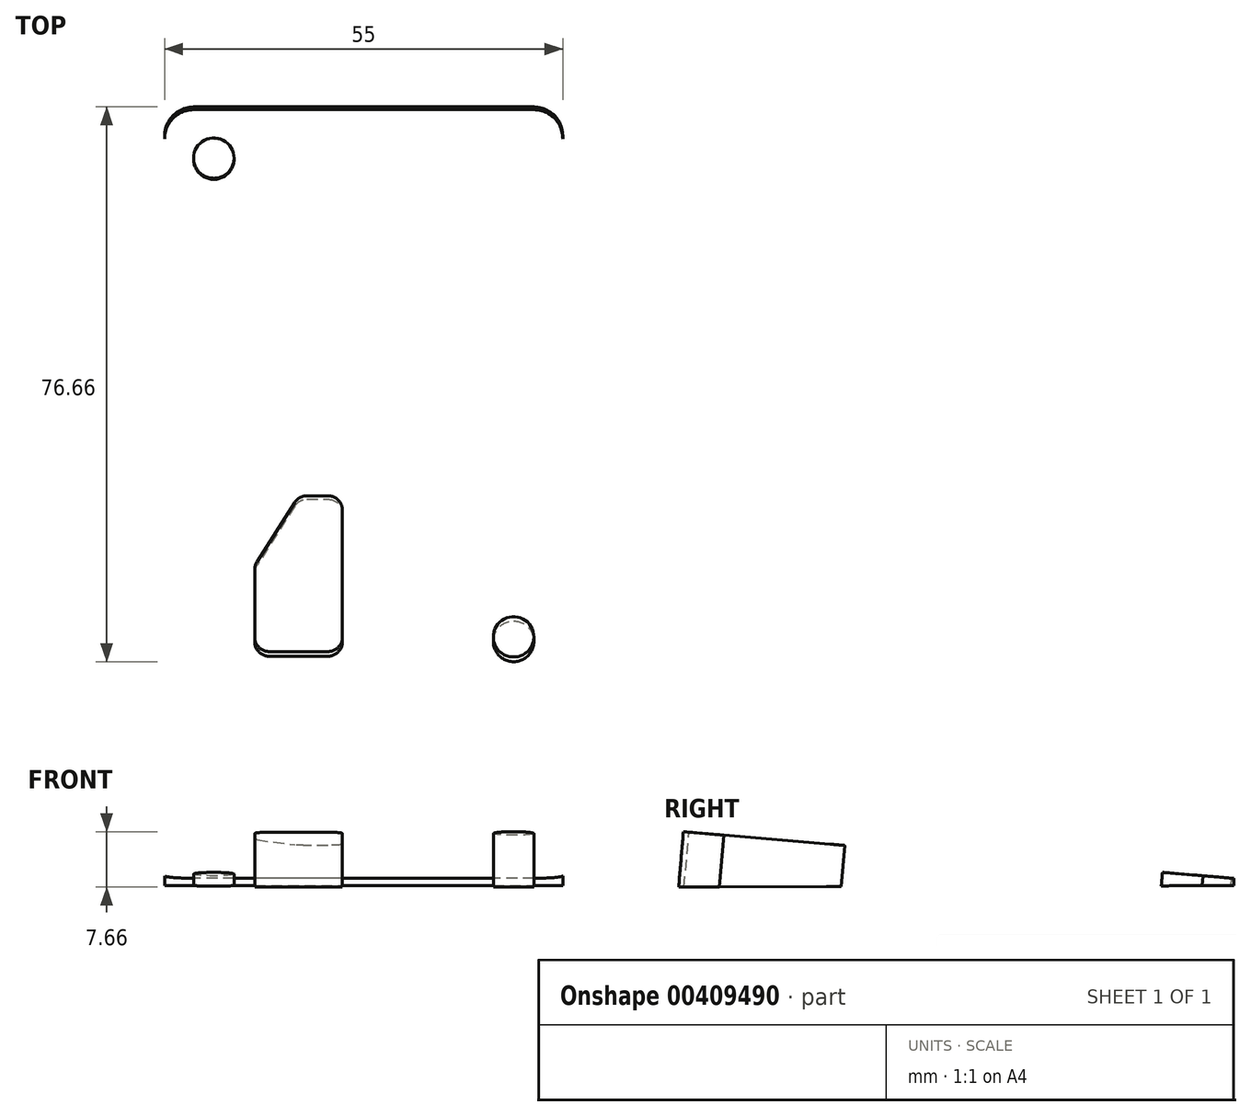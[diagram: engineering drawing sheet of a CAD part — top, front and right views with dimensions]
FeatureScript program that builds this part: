
annotation { "Feature Type Name" : "Feature", "Feature Type Description" : "" }
export const myFeature = defineFeature(function(context is Context, id is Id, definition is map)
    precondition{}
    {
        {
            var Q0;
            Q0=qCreatedBy(makeId("Right.planeOp"),FACE);
            var sketch = newSketch(context, id + "F0", { "sketchPlane" : qUnion([Q0])});
            skLineSegment(sketch, "E0", {"start": v(-0.45, -1.5) * mm, "end": v(-0.45, 6.5) * mm});
            skLineSegment(sketch, "E1", {"start": v(-0.45, 6.5) * mm, "end": v(79.55, -0.3) * mm});
            skLineSegment(sketch, "E2", {"start": v(79.55, -0.3) * mm, "end": v(79.55, -1.3) * mm});
            skLineSegment(sketch, "E3", {"start": v(79.55, -1.3) * mm, "end": v(-0.45, -1.5) * mm});
            skSolve(sketch);
        }
        {
            var Q0;
            Q0=makeQuery(id+"F0.imprint","IMPRINT",FACE,{"disambiguationData":[TD([[makeQuery(id+"F0.imprint","IMPRINT",EDGE,{"derivedFrom":sQuery(id+"F0.wireOp",EDGE,"E0")}),-1.0]])]});
            extrude(context, id + "F1", {"entities" : qUnion([Q0]), "depth" : 55 * mm});
        }
        {
            var Q0;
            Q0=makeQuery(id+"F1.opExtrude","CAP_EDGE",EDGE,{"disambiguationData":[OSD([sQuery(id+"F0.wireOp",EDGE,"E0")])],"isStart":true});
            var Q1;
            Q1=makeQuery(id+"F1.opExtrude","CAP_EDGE",EDGE,{"disambiguationData":[OSD([sQuery(id+"F0.wireOp",EDGE,"E0")])],"isStart":false});
            var Q2;
            Q2=makeQuery(id+"F1.opExtrude","CAP_EDGE",EDGE,{"disambiguationData":[OSD([sQuery(id+"F0.wireOp",EDGE,"E2")])],"isStart":true});
            var Q3;
            Q3=makeQuery(id+"F1.opExtrude","CAP_EDGE",EDGE,{"disambiguationData":[OSD([sQuery(id+"F0.wireOp",EDGE,"E2")])],"isStart":false});
            fillet(context, id + "F2", {"entities" : qUnion([Q0, Q1, Q2, Q3]), "radius" : 4 * mm, "tangentPropagation" : true, "allowEdgeOverflow" : false});
        }
        {
            var Q0;
            Q0=makeQuery(id+"F1.opExtrude","SWEPT_FACE",FACE,{"disambiguationData":[OSD([sQuery(id+"F0.wireOp",EDGE,"E1")])]});
            var sketch = newSketch(context, id + "F3", { "sketchPlane" : qUnion([Q0])});
            skLineSegment(sketch, "E4.bottom", {"start": v(51, -1) * mm, "end": v(4, -1) * mm});
            skLineSegment(sketch, "E4.top", {"start": v(51, 79) * mm, "end": v(4, 79) * mm});
            skLineSegment(sketch, "E4.left", {"start": v(55, 3) * mm, "end": v(55, 75) * mm});
            skLineSegment(sketch, "E4.right", {"start": v(0, 3) * mm, "end": v(0, 75) * mm});
            skCircle(sketch, "E5", {"center": v(6.8, 5.8) * mm, "radius": 2.8 * mm});
            skCircle(sketch, "E6.MirrorC", {"center": v(48.2, 5.8) * mm, "radius": 2.8 * mm});
            skCircle(sketch, "E7.MirrorC", {"center": v(48.2, 72.2) * mm, "radius": 2.8 * mm});
            skCircle(sketch, "E8.MirrorC", {"center": v(6.8, 72.2) * mm, "radius": 2.8 * mm});
            skLineSegment(sketch, "E9.bottom", {"start": v(35.5, 29) * mm, "end": v(19.5, 29) * mm});
            skLineSegment(sketch, "E9.top", {"start": v(35.5, 49) * mm, "end": v(19.5, 49) * mm});
            skLineSegment(sketch, "E9.left", {"start": v(37.5, 31) * mm, "end": v(37.5, 47) * mm});
            skLineSegment(sketch, "E9.right", {"start": v(17.5, 31) * mm, "end": v(17.5, 47) * mm});
            skArc(sketch, "E10.filletArc", {"start": v(19.5, 49) * mm, "mid": v(18.09, 48.42) * mm, "end": v(17.5, 47) * mm});
            skArc(sketch, "E11.filletArc", {"start": v(37.5, 47) * mm, "mid": v(36.91, 48.42) * mm, "end": v(35.5, 49) * mm});
            skArc(sketch, "E12.filletArc", {"start": v(17.5, 31) * mm, "mid": v(18.09, 29.59) * mm, "end": v(19.5, 29) * mm});
            skArc(sketch, "E13.filletArc", {"start": v(35.5, 29) * mm, "mid": v(36.91, 29.59) * mm, "end": v(37.5, 31) * mm});
            skArc(sketch, "E14.filletArc", {"start": v(0, 3) * mm, "mid": v(1.17, 0.17) * mm, "end": v(4, -1) * mm});
            skArc(sketch, "E15.filletArc", {"start": v(51, -1) * mm, "mid": v(53.83, 0.17) * mm, "end": v(55, 3) * mm});
            skArc(sketch, "E16.filletArc", {"start": v(4, 79) * mm, "mid": v(1.17, 77.83) * mm, "end": v(0, 75) * mm});
            skArc(sketch, "E17.filletArc", {"start": v(55, 75) * mm, "mid": v(53.83, 77.83) * mm, "end": v(51, 79) * mm});
            skLineSegment(sketch, "E18.bottom", {"start": v(14.45, 74.25) * mm, "end": v(22.57, 74.25) * mm});
            skLineSegment(sketch, "E18.right", {"start": v(24.57, 72.25) * mm, "end": v(24.57, 54.64) * mm});
            skArc(sketch, "E19.filletArc", {"start": v(14.45, 74.25) * mm, "mid": v(13.04, 73.67) * mm, "end": v(12.45, 72.25) * mm});
            skArc(sketch, "E20.filletArc", {"start": v(22.57, 52.64) * mm, "mid": v(23.98, 53.23) * mm, "end": v(24.57, 54.64) * mm});
            skArc(sketch, "E21.filletArc", {"start": v(24.57, 72.25) * mm, "mid": v(23.98, 73.67) * mm, "end": v(22.57, 74.25) * mm});
            skLineSegment(sketch, "E22", {"start": v(12.45, 72.25) * mm, "end": v(12.45, 62.83) * mm});
            skLineSegment(sketch, "E23", {"start": v(12.76, 61.76) * mm, "end": v(17.98, 53.57) * mm});
            skLineSegment(sketch, "E24", {"start": v(22.57, 52.64) * mm, "end": v(19.66, 52.64) * mm});
            skArc(sketch, "E25.filletArc", {"start": v(12.45, 62.83) * mm, "mid": v(12.53, 62.28) * mm, "end": v(12.76, 61.76) * mm});
            skArc(sketch, "E26.filletArc", {"start": v(17.98, 53.57) * mm, "mid": v(18.7, 52.89) * mm, "end": v(19.66, 52.64) * mm});
            skLineSegment(sketch, "E27.MirrorCS", {"start": v(30.43, 72.25) * mm, "end": v(30.43, 54.64) * mm});
            skLineSegment(sketch, "E28.MirrorCS", {"start": v(42.55, 72.25) * mm, "end": v(42.55, 62.83) * mm});
            skArc(sketch, "E29.MirrorCS", {"start": v(40.55, 74.25) * mm, "mid": v(41.96, 73.67) * mm, "end": v(42.55, 72.25) * mm});
            skLineSegment(sketch, "E30.MirrorCS", {"start": v(40.55, 74.25) * mm, "end": v(32.43, 74.25) * mm});
            skArc(sketch, "E31.MirrorCS", {"start": v(30.43, 72.25) * mm, "mid": v(31.02, 73.67) * mm, "end": v(32.43, 74.25) * mm});
            skArc(sketch, "E32.MirrorCS", {"start": v(32.43, 52.64) * mm, "mid": v(31.02, 53.23) * mm, "end": v(30.43, 54.64) * mm});
            skLineSegment(sketch, "E33.MirrorCS", {"start": v(32.43, 52.64) * mm, "end": v(35.34, 52.64) * mm});
            skLineSegment(sketch, "E34.MirrorCS", {"start": v(42.24, 61.76) * mm, "end": v(37.02, 53.57) * mm});
            skArc(sketch, "E35.MirrorCS", {"start": v(42.55, 62.83) * mm, "mid": v(42.47, 62.28) * mm, "end": v(42.24, 61.76) * mm});
            skArc(sketch, "E36.MirrorCS", {"start": v(37.02, 53.57) * mm, "mid": v(36.3, 52.89) * mm, "end": v(35.34, 52.64) * mm});
            skLineSegment(sketch, "E37.MirrorCS", {"start": v(30.43, 5.75) * mm, "end": v(30.43, 23.36) * mm});
            skArc(sketch, "E38.MirrorCS", {"start": v(32.43, 25.36) * mm, "mid": v(31.02, 24.78) * mm, "end": v(30.43, 23.36) * mm});
            skLineSegment(sketch, "E39.MirrorCS", {"start": v(32.43, 25.36) * mm, "end": v(35.34, 25.36) * mm});
            skArc(sketch, "E40.MirrorCS", {"start": v(37.02, 24.44) * mm, "mid": v(36.3, 25.12) * mm, "end": v(35.34, 25.36) * mm});
            skLineSegment(sketch, "E41.MirrorCS", {"start": v(42.24, 16.24) * mm, "end": v(37.02, 24.44) * mm});
            skArc(sketch, "E42.MirrorCS", {"start": v(42.55, 15.17) * mm, "mid": v(42.47, 15.73) * mm, "end": v(42.24, 16.24) * mm});
            skLineSegment(sketch, "E43.MirrorCS", {"start": v(42.55, 5.75) * mm, "end": v(42.55, 15.17) * mm});
            skArc(sketch, "E44.MirrorCS", {"start": v(30.43, 5.75) * mm, "mid": v(31.02, 4.34) * mm, "end": v(32.43, 3.75) * mm});
            skLineSegment(sketch, "E45.MirrorCS", {"start": v(40.55, 3.75) * mm, "end": v(32.43, 3.75) * mm});
            skArc(sketch, "E46.MirrorCS", {"start": v(40.55, 3.75) * mm, "mid": v(41.96, 4.34) * mm, "end": v(42.55, 5.75) * mm});
            skArc(sketch, "E47.MirrorCS", {"start": v(24.57, 5.75) * mm, "mid": v(23.98, 4.34) * mm, "end": v(22.57, 3.75) * mm});
            skLineSegment(sketch, "E48.MirrorCS", {"start": v(24.57, 5.75) * mm, "end": v(24.57, 23.36) * mm});
            skLineSegment(sketch, "E49.MirrorCS", {"start": v(14.45, 3.75) * mm, "end": v(22.57, 3.75) * mm});
            skArc(sketch, "E50.MirrorCS", {"start": v(14.45, 3.75) * mm, "mid": v(13.04, 4.34) * mm, "end": v(12.45, 5.75) * mm});
            skLineSegment(sketch, "E51.MirrorCS", {"start": v(12.45, 5.75) * mm, "end": v(12.45, 15.17) * mm});
            skArc(sketch, "E52.MirrorCS", {"start": v(12.45, 15.17) * mm, "mid": v(12.53, 15.73) * mm, "end": v(12.76, 16.24) * mm});
            skLineSegment(sketch, "E53.MirrorCS", {"start": v(12.76, 16.24) * mm, "end": v(17.98, 24.44) * mm});
            skArc(sketch, "E54.MirrorCS", {"start": v(22.57, 25.36) * mm, "mid": v(23.98, 24.78) * mm, "end": v(24.57, 23.36) * mm});
            skLineSegment(sketch, "E55.MirrorCS", {"start": v(22.57, 25.36) * mm, "end": v(19.66, 25.36) * mm});
            skArc(sketch, "E56.MirrorCS", {"start": v(17.98, 24.44) * mm, "mid": v(18.7, 25.12) * mm, "end": v(19.66, 25.36) * mm});
            skLineSegment(sketch, "E57.bottom", {"start": v(9.25, 52.5) * mm, "end": v(10.5, 52.5) * mm});
            skLineSegment(sketch, "E57.top", {"start": v(9.25, 23.36) * mm, "end": v(10.5, 23.36) * mm});
            skLineSegment(sketch, "E57.left", {"start": v(4.25, 47.5) * mm, "end": v(4.25, 28.36) * mm});
            skLineSegment(sketch, "E57.right", {"start": v(15.5, 47.5) * mm, "end": v(15.5, 28.36) * mm});
            skArc(sketch, "E58.filletArc", {"start": v(4.25, 28.36) * mm, "mid": v(5.71, 24.83) * mm, "end": v(9.25, 23.36) * mm});
            skArc(sketch, "E59.filletArc", {"start": v(10.5, 23.36) * mm, "mid": v(14.04, 24.83) * mm, "end": v(15.5, 28.36) * mm});
            skArc(sketch, "E60.filletArc", {"start": v(9.25, 52.5) * mm, "mid": v(5.71, 51.04) * mm, "end": v(4.25, 47.5) * mm});
            skArc(sketch, "E61.filletArc", {"start": v(15.5, 47.5) * mm, "mid": v(14.04, 51.04) * mm, "end": v(10.5, 52.5) * mm});
            skLineSegment(sketch, "E62.MirrorCS", {"start": v(50.75, 47.5) * mm, "end": v(50.75, 28.36) * mm});
            skLineSegment(sketch, "E63.MirrorCS", {"start": v(39.5, 47.5) * mm, "end": v(39.5, 28.36) * mm});
            skArc(sketch, "E64.MirrorCS", {"start": v(39.5, 47.5) * mm, "mid": v(40.96, 51.04) * mm, "end": v(44.5, 52.5) * mm});
            skLineSegment(sketch, "E65.MirrorCS", {"start": v(45.75, 52.5) * mm, "end": v(44.5, 52.5) * mm});
            skArc(sketch, "E66.MirrorCS", {"start": v(45.75, 52.5) * mm, "mid": v(49.29, 51.04) * mm, "end": v(50.75, 47.5) * mm});
            skArc(sketch, "E67.MirrorCS", {"start": v(50.75, 28.36) * mm, "mid": v(49.29, 24.83) * mm, "end": v(45.75, 23.36) * mm});
            skArc(sketch, "E68.MirrorCS", {"start": v(44.5, 23.36) * mm, "mid": v(40.96, 24.83) * mm, "end": v(39.5, 28.36) * mm});
            skLineSegment(sketch, "E69.MirrorCS", {"start": v(45.75, 23.36) * mm, "end": v(44.5, 23.36) * mm});
            skSolve(sketch);
        }
        {
            var Q0;
            Q0=makeQuery(id+"F3.imprint","IMPRINT",FACE,{"disambiguationData":[TD([[makeQuery(id+"F3.imprint","IMPRINT",EDGE,{"derivedFrom":sQuery(id+"F3.wireOp",EDGE,"E57.bottom")}),-1.0]])]});
            var Q1;
            Q1=makeQuery(id+"F3.imprint","IMPRINT",FACE,{"disambiguationData":[TD([[makeQuery(id+"F3.imprint","IMPRINT",EDGE,{"derivedFrom":sQuery(id+"F3.wireOp",EDGE,"E9.bottom")}),-1.0]])]});
            var Q2;
            Q2=makeQuery(id+"F3.imprint","IMPRINT",FACE,{"disambiguationData":[TD([[makeQuery(id+"F3.imprint","IMPRINT",EDGE,{"derivedFrom":sQuery(id+"F3.wireOp",EDGE,"E62.MirrorCS")}),-1.0]])]});
            var Q3;
            Q3=makeQuery(id+"F3.imprint","IMPRINT",FACE,{"disambiguationData":[TD([[makeQuery(id+"F3.imprint","IMPRINT",EDGE,{"derivedFrom":sQuery(id+"F3.wireOp",EDGE,"E47.MirrorCS")}),-1.0]])]});
            var Q4;
            Q4=makeQuery(id+"F3.imprint","IMPRINT",FACE,{"disambiguationData":[TD([[makeQuery(id+"F3.imprint","IMPRINT",EDGE,{"derivedFrom":sQuery(id+"F3.wireOp",EDGE,"E37.MirrorCS")}),-1.0]])]});
            var Q5;
            Q5=makeQuery(id+"F3.imprint","IMPRINT",FACE,{"disambiguationData":[TD([[makeQuery(id+"F3.imprint","IMPRINT",EDGE,{"derivedFrom":sQuery(id+"F3.wireOp",EDGE,"E27.MirrorCS")}),1.0]])]});
            var Q6;
            Q6=makeQuery(id+"F3.imprint","IMPRINT",FACE,{"disambiguationData":[TD([[makeQuery(id+"F3.imprint","IMPRINT",EDGE,{"derivedFrom":sQuery(id+"F3.wireOp",EDGE,"E18.bottom")}),-1.0]])]});
            var Q7;
            Q7=makeQuery(id+"F3.imprint","IMPRINT",FACE,{"disambiguationData":[TD([[makeQuery(id+"F3.imprint","IMPRINT",EDGE,{"derivedFrom":sQuery(id+"F3.wireOp",EDGE,"E7.MirrorC")}),1.0]])]});
            var Q8;
            Q8=makeQuery(id+"F3.imprint","IMPRINT",FACE,{"disambiguationData":[TD([[makeQuery(id+"F3.imprint","IMPRINT",EDGE,{"derivedFrom":sQuery(id+"F3.wireOp",EDGE,"E6.MirrorC")}),-1.0]])]});
            var Q9;
            Q9=makeQuery(id+"F3.imprint","IMPRINT",FACE,{"disambiguationData":[TD([[makeQuery(id+"F3.imprint","IMPRINT",EDGE,{"derivedFrom":sQuery(id+"F3.wireOp",EDGE,"E5")}),1.0]])]});
            var Q10;
            Q10=makeQuery(id+"F3.imprint","IMPRINT",FACE,{"disambiguationData":[TD([[makeQuery(id+"F3.imprint","IMPRINT",EDGE,{"derivedFrom":sQuery(id+"F3.wireOp",EDGE,"E8.MirrorC")}),-1.0]])]});
            extrude(context, id + "F4", {"entities" : qUnion([Q0, Q1, Q2, Q3, Q4, Q5, Q6, Q7, Q8, Q9, Q10]), "operationType" : NewBodyOperationType.REMOVE, "oppositeDirection" : true, "depth" : 25 * mm});
        }
    });
